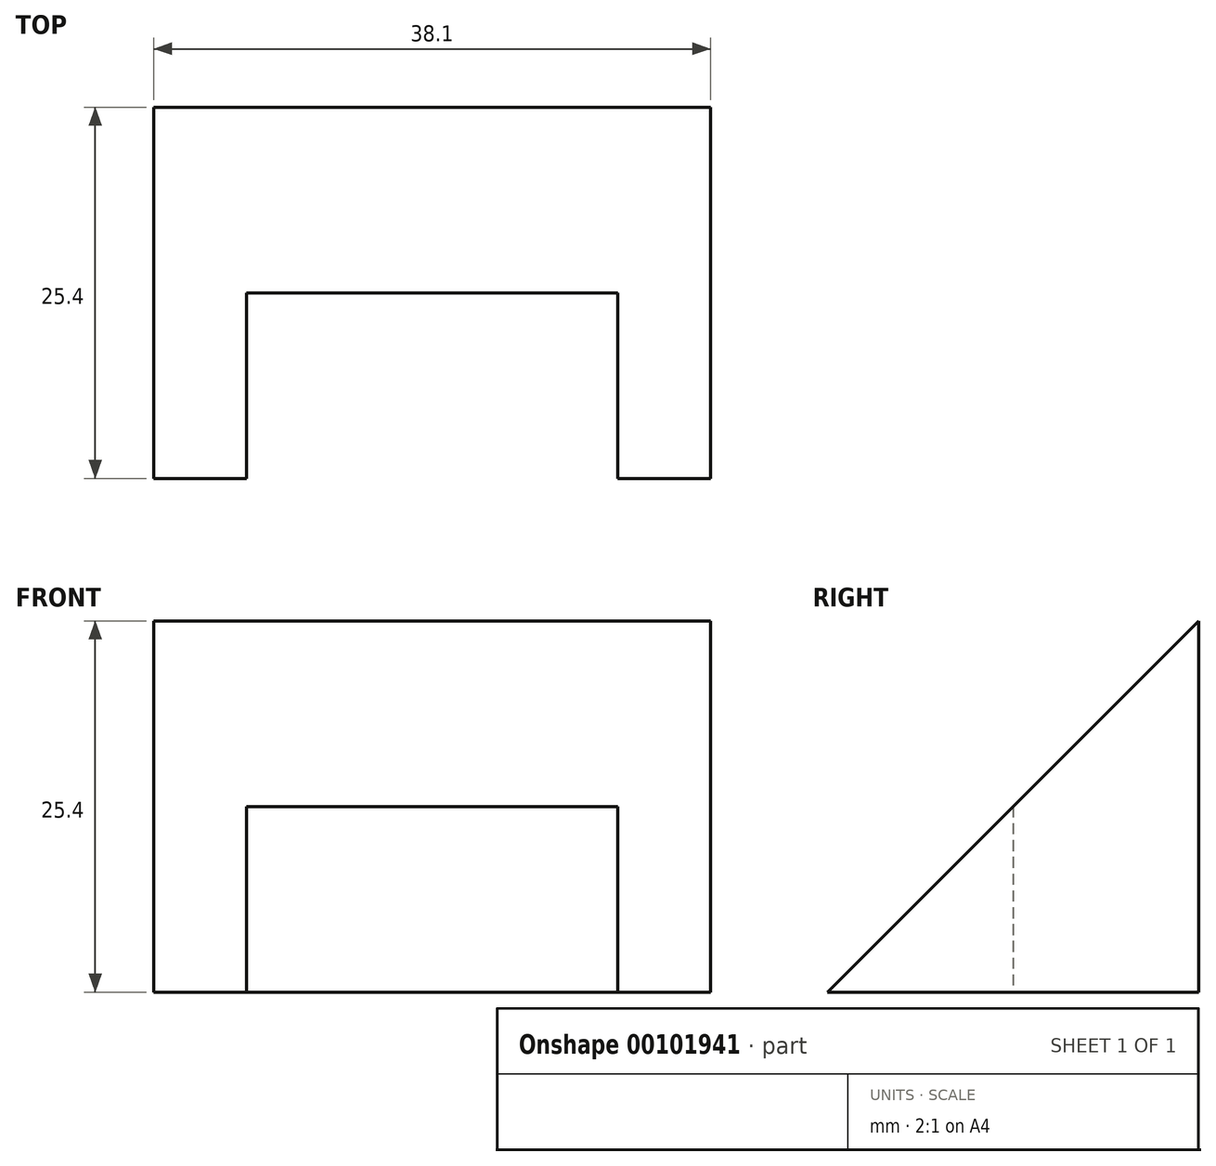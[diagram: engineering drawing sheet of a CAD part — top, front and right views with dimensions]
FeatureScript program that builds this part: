
annotation { "Feature Type Name" : "Feature", "Feature Type Description" : "" }
export const myFeature = defineFeature(function(context is Context, id is Id, definition is map)
    precondition{}
    {
        {
            var Q0;
            Q0=qCreatedBy(makeId("Right.planeOp"),FACE);
            var sketch = newSketch(context, id + "F0", { "sketchPlane" : qUnion([Q0])});
            skLineSegment(sketch, "E0", {"start": v(0, 0) * mm, "end": v(-25.4, 0) * mm});
            skLineSegment(sketch, "E1", {"start": v(-25.4, 0) * mm, "end": v(0, 25.4) * mm});
            skLineSegment(sketch, "E2", {"start": v(0, 25.4) * mm, "end": v(0, 0) * mm});
            skSolve(sketch);
        }
        {
            var Q0;
            Q0 = qSketchRegion(id + "F0", true);
            extrude(context, id + "F1", {"entities" : qUnion([Q0]), "endBound" : BoundingType.SYMMETRIC, "oppositeDirection" : true, "depth" : 38.1 * mm});
        }
        {
            var Q0;
            Q0=makeQuery(id+"F1.opExtrude","CAP_FACE",FACE,{"disambiguationData":[OSD([sQuery(id+"F0.wireOp",EDGE,"E0"),sQuery(id+"F0.wireOp",EDGE,"E1"),sQuery(id+"F0.wireOp",EDGE,"E2")])],"isStart":true});
            var sketch = newSketch(context, id + "F2", { "sketchPlane" : qUnion([Q0])});
            skLineSegment(sketch, "E3", {"start": v(-12.7, 12.7) * mm, "end": v(-12.7, 0) * mm});
            skSolve(sketch);
        }
        {
            var Q0;
            {var subQ0=sQuery(id+"F2.wireOp",EDGE,"E3");Q0=makeQuery(id+"F2.imprint","IMPRINT",FACE,{"disambiguationData":[TD([[makeQuery(id+"F2.imprint","IMPRINT",EDGE,{"derivedFrom":subQ0}),-1.0]])]});}
            extrude(context, id + "F3", {"entities" : qUnion([Q0]), "operationType" : NewBodyOperationType.REMOVE, "oppositeDirection" : true, "depth" : 31.75 * mm, "hasSecondDirection" : true, "secondDirectionOppositeDirection" : true, "secondDirectionDepth" : 6.35 * mm});
        }
    });
